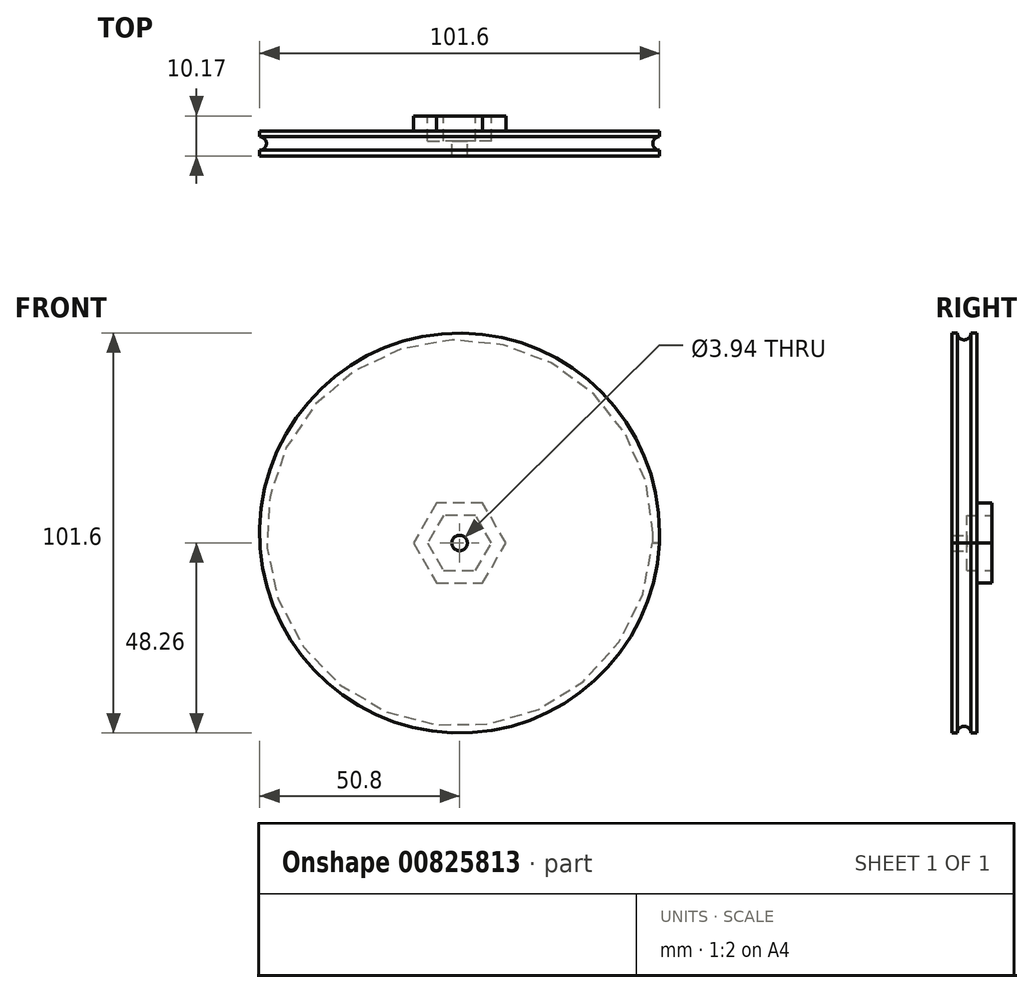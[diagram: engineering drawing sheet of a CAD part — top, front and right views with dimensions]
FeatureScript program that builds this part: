
annotation { "Feature Type Name" : "Feature", "Feature Type Description" : "" }
export const myFeature = defineFeature(function(context is Context, id is Id, definition is map)
    precondition{}
    {
        {
            var Q0;
            Q0=qCreatedBy(makeId("Top.planeOp"),FACE);
            var sketch = newSketch(context, id + "F0", { "sketchPlane" : qUnion([Q0])});
            skLineSegment(sketch, "E0.bottom", {"start": v(0, 3.18) * mm, "end": v(50.8, 3.17) * mm});
            skLineSegment(sketch, "E0.top", {"start": v(0, -3.18) * mm, "end": v(50.8, -3.18) * mm});
            skLineSegment(sketch, "E0.left", {"start": v(0, 3.18) * mm, "end": v(0, -3.18) * mm});
            skLineSegment(sketch, "E0.right", {"start": v(50.8, 3.18) * mm, "end": v(50.8, -3.18) * mm});
            skSolve(sketch);
        }
        {
            var Q0;
            Q0=makeQuery(id+"F0.imprint","IMPRINT",FACE,{"disambiguationData":[TD([[makeQuery(id+"F0.imprint","IMPRINT",EDGE,{"derivedFrom":sQuery(id+"F0.wireOp",EDGE,"E0.bottom")}),-1.0]])]});
            extrude(context, id + "F1", {"entities" : qUnion([Q0]), "depth" : 2.54 * mm, "offsetDistance" : 25.4 * mm});
        }
        {
            var Q0;
            Q0=makeQuery(id+"F1.opExtrude","CAP_FACE",FACE,{"disambiguationData":[OSD([sQuery(id+"F0.wireOp",EDGE,"E0.bottom"),sQuery(id+"F0.wireOp",EDGE,"E0.top"),sQuery(id+"F0.wireOp",EDGE,"E0.left"),sQuery(id+"F0.wireOp",EDGE,"E0.right")])],"isStart":false});
            var sketch = newSketch(context, id + "F2", { "sketchPlane" : qUnion([Q0])});
            skCircle(sketch, "E1", {"center": v(50.8, 0) * mm, "radius": 1.72 * mm});
            skSolve(sketch);
        }
        {
            var Q0;
            {var subQ0=sQuery(id+"F2.wireOp",EDGE,"E1");var subQ1=makeQuery(id+"F1.opExtrude","CAP_EDGE",EDGE,{"disambiguationData":[OSD([sQuery(id+"F0.wireOp",EDGE,"E0.right")])],"isStart":false});var subQ2=makeQuery(id+"F2.imprint","INTERSECT",VERTEX,{"disambiguationData":[OD(0.0)],"derivedFrom":[subQ1,subQ0]});Q0=makeQuery(id+"F2.imprint","IMPRINT",FACE,{"disambiguationData":[TD([[makeQuery(id+"F2.imprint","IMPRINT",EDGE,{"disambiguationData":[TD([[subQ2,-1.0]])],"derivedFrom":subQ0}),1.0]])]});}
            extrude(context, id + "F3", {"entities" : qUnion([Q0]), "operationType" : NewBodyOperationType.REMOVE, "oppositeDirection" : true, "depth" : 2.54 * mm, "offsetDistance" : 25.4 * mm});
        }
        {
            var Q0;
            Q0=makeQuery(id+"F1.opExtrude","CAP_FACE",FACE,{"disambiguationData":[OSD([sQuery(id+"F0.wireOp",EDGE,"E0.bottom"),sQuery(id+"F0.wireOp",EDGE,"E0.top"),sQuery(id+"F0.wireOp",EDGE,"E0.left"),sQuery(id+"F0.wireOp",EDGE,"E0.right")])],"isStart":false});
            var Q1;
            Q1=makeQuery(id+"F1.opExtrude","CAP_EDGE",EDGE,{"disambiguationData":[OSD([sQuery(id+"F0.wireOp",EDGE,"E0.left")])],"isStart":false});
            revolve(context, id + "F4", {"operationType" : NewBodyOperationType.ADD, "surfaceOperationType" : NewSurfaceOperationType.NEW, "entities" : qUnion([Q0]), "axis" : qUnion([Q1]), "revolveType" : RevolveType.FULL});
        }
        {
            var Q0;
            {var subQ0=sQuery(id+"F0.wireOp",EDGE,"E0.bottom");Q0=makeQuery(id+"F4.boolean.opBoolean","MERGE",FACE,{"derivedFrom":[makeQuery(id+"F1.opExtrude","SWEPT_FACE",FACE,{"disambiguationData":[OSD([subQ0])]}),makeQuery(id+"F4.opRevolve","SWEPT_FACE",FACE,{"disambiguationData":[OSD([subQ0])]})]});}
            var sketch = newSketch(context, id + "F5", { "sketchPlane" : qUnion([Q0])});
            skCircle(sketch, "E2.cCircle", {"center": v(0, 0) * mm, "radius": 10.16 * mm, "construction": true});
            skLineSegment(sketch, "E2.0", {"start": v(-5.87, 10.16) * mm, "end": v(5.87, 10.16) * mm});
            skLineSegment(sketch, "E2.1", {"start": v(5.87, 10.16) * mm, "end": v(11.73, 0) * mm});
            skLineSegment(sketch, "E2.2", {"start": v(11.73, 0) * mm, "end": v(5.87, -10.16) * mm});
            skLineSegment(sketch, "E2.3", {"start": v(5.87, -10.16) * mm, "end": v(-5.87, -10.16) * mm});
            skLineSegment(sketch, "E2.4", {"start": v(-5.87, -10.16) * mm, "end": v(-11.73, 0) * mm});
            skLineSegment(sketch, "E2.5", {"start": v(-11.73, 0) * mm, "end": v(-5.87, 10.16) * mm});
            skPoint(sketch, "E2.0.midPoint", {"position": v(0, 10.16) * mm});
            skSolve(sketch);
        }
        {
            var Q0;
            Q0=makeQuery(id+"F5.imprint","IMPRINT",FACE,{"disambiguationData":[TD([[makeQuery(id+"F5.imprint","IMPRINT",EDGE,{"derivedFrom":sQuery(id+"F5.wireOp",EDGE,"E2.0")}),-1.0]])]});
            extrude(context, id + "F6", {"entities" : qUnion([Q0]), "operationType" : NewBodyOperationType.ADD, "depth" : 3.8 * mm, "offsetDistance" : 25.4 * mm});
        }
        {
            var Q0;
            Q0=makeQuery(id+"F6.opExtrude","CAP_FACE",FACE,{"disambiguationData":[OSD([sQuery(id+"F5.wireOp",EDGE,"E2.0"),sQuery(id+"F5.wireOp",EDGE,"E2.1"),sQuery(id+"F5.wireOp",EDGE,"E2.2"),sQuery(id+"F5.wireOp",EDGE,"E2.3"),sQuery(id+"F5.wireOp",EDGE,"E2.4"),sQuery(id+"F5.wireOp",EDGE,"E2.5")])],"isStart":false});
            var sketch = newSketch(context, id + "F7", { "sketchPlane" : qUnion([Q0])});
            skCircle(sketch, "E3.cCircle", {"center": v(0, 0) * mm, "radius": 7.02 * mm, "construction": true});
            skLineSegment(sketch, "E3.0", {"start": v(-4.05, 7.02) * mm, "end": v(4.05, 7.02) * mm});
            skLineSegment(sketch, "E3.1", {"start": v(4.05, 7.02) * mm, "end": v(8.1, 0) * mm});
            skLineSegment(sketch, "E3.2", {"start": v(8.1, 0) * mm, "end": v(4.05, -7.02) * mm});
            skLineSegment(sketch, "E3.3", {"start": v(4.05, -7.02) * mm, "end": v(-4.05, -7.02) * mm});
            skLineSegment(sketch, "E3.4", {"start": v(-4.05, -7.02) * mm, "end": v(-8.1, 0) * mm});
            skLineSegment(sketch, "E3.5", {"start": v(-8.1, 0) * mm, "end": v(-4.05, 7.02) * mm});
            skPoint(sketch, "E3.0.midPoint", {"position": v(0, 7.02) * mm});
            skSolve(sketch);
        }
        {
            var Q0;
            Q0=makeQuery(id+"F7.imprint","IMPRINT",FACE,{"disambiguationData":[TD([[makeQuery(id+"F7.imprint","IMPRINT",EDGE,{"derivedFrom":sQuery(id+"F7.wireOp",EDGE,"E3.0")}),-1.0]])]});
            extrude(context, id + "F8", {"entities" : qUnion([Q0]), "operationType" : NewBodyOperationType.REMOVE, "oppositeDirection" : true, "depth" : 6.35 * mm, "offsetDistance" : 25.4 * mm});
        }
        {
            var Q0;
            Q0=makeQuery(id+"F8.boolean.opBoolean","COPY",FACE,{"derivedFrom":makeQuery(id+"F8.opExtrude","CAP_FACE",FACE,{"disambiguationData":[OSD([sQuery(id+"F7.wireOp",EDGE,"E3.0"),sQuery(id+"F7.wireOp",EDGE,"E3.1"),sQuery(id+"F7.wireOp",EDGE,"E3.2"),sQuery(id+"F7.wireOp",EDGE,"E3.3"),sQuery(id+"F7.wireOp",EDGE,"E3.4"),sQuery(id+"F7.wireOp",EDGE,"E3.5")])],"isStart":false})});
            var sketch = newSketch(context, id + "F9", { "sketchPlane" : qUnion([Q0])});
            skCircle(sketch, "E4", {"center": v(0, 0) * mm, "radius": 1.97 * mm});
            skSolve(sketch);
        }
        {
            var Q0;
            Q0=makeQuery(id+"F9.imprint","IMPRINT",FACE,{"disambiguationData":[TD([[makeQuery(id+"F9.imprint","IMPRINT",EDGE,{"derivedFrom":sQuery(id+"F9.wireOp",EDGE,"E4")}),1.0]])]});
            var Q1;
            Q1=sQuery(id+"F9.wireOp",EDGE,"E4");
            extrude(context, id + "F10", {"entities" : qUnion([Q0]), "operationType" : NewBodyOperationType.REMOVE, "surfaceEntities" : qUnion([Q1]), "oppositeDirection" : true, "depth" : 6.35 * mm, "offsetDistance" : 25.4 * mm});
        }
    });
